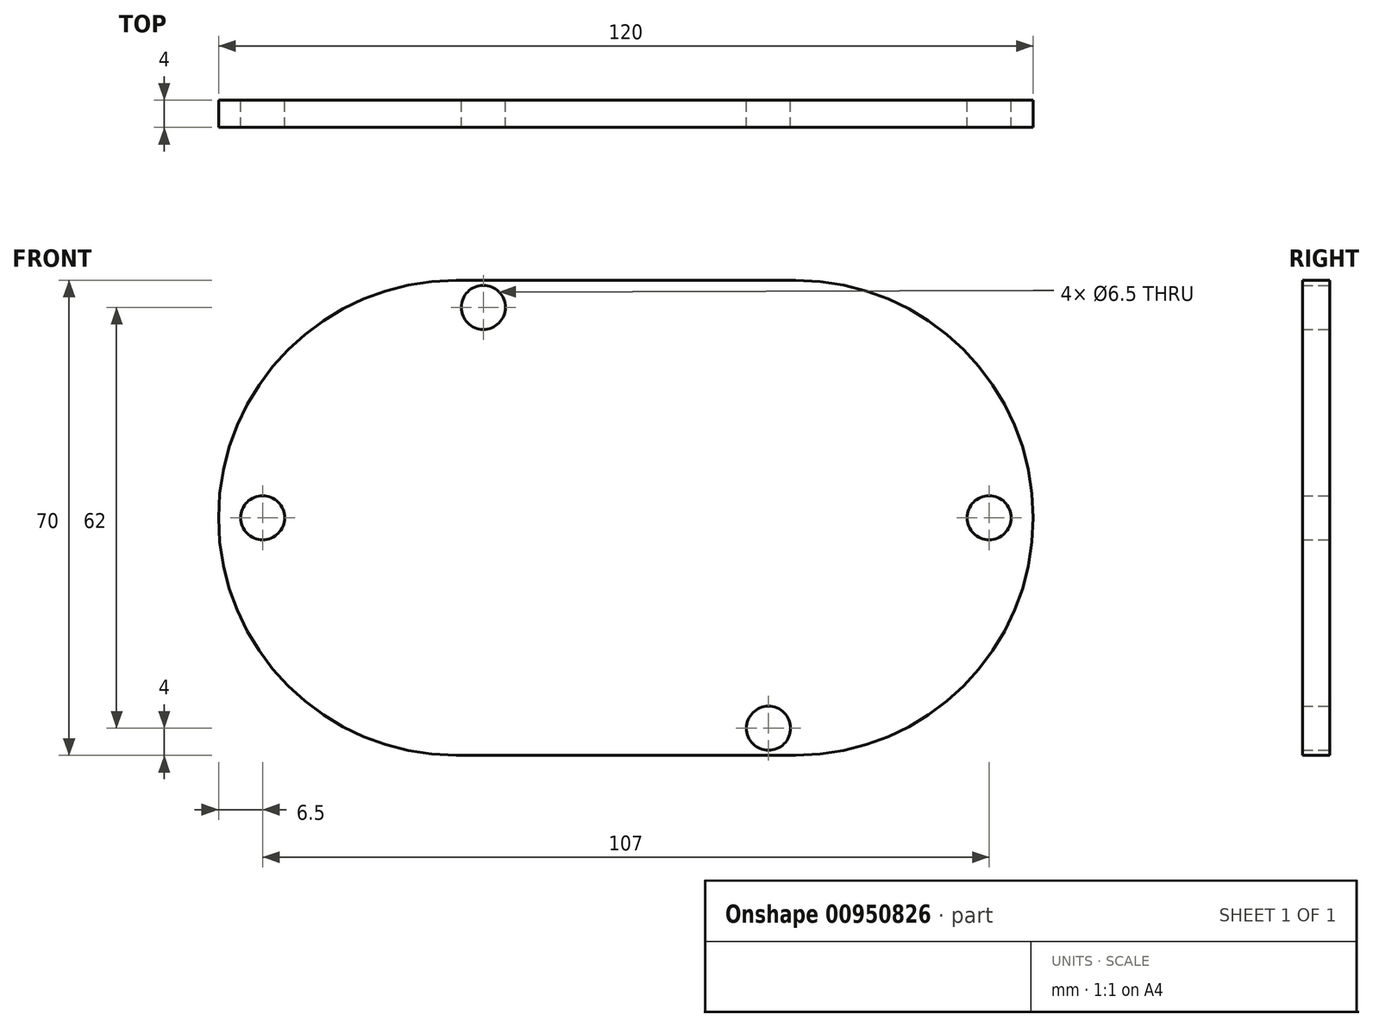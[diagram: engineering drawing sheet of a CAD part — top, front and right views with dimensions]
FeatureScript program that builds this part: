
annotation { "Feature Type Name" : "Feature", "Feature Type Description" : "" }
export const myFeature = defineFeature(function(context is Context, id is Id, definition is map)
    precondition{}
    {
        {
            var Q0;
            Q0=qCreatedBy(makeId("Front.planeOp"),FACE);
            var sketch = newSketch(context, id + "F0", { "sketchPlane" : qUnion([Q0])});
            skLineSegment(sketch, "E0", {"start": v(-25, 35) * mm, "end": v(25, 35) * mm});
            skLineSegment(sketch, "E1", {"start": v(-25, -35) * mm, "end": v(25, -35) * mm});
            skArc(sketch, "E2", {"start": v(25, -35) * mm, "mid": v(60, 0) * mm, "end": v(25, 35) * mm});
            skArc(sketch, "E3", {"start": v(-25, 35) * mm, "mid": v(-60, 0) * mm, "end": v(-25, -35) * mm});
            skSolve(sketch);
        }
        {
            var Q0;
            Q0=qSketchRegion(id+"F0",true);
            extrude(context, id + "F1", {"entities" : qUnion([Q0]), "depth" : 4 * mm, "offsetDistance" : 25 * mm});
        }
        {
            var Q0;
            Q0=qCreatedBy(makeId("Front.planeOp"),FACE);
            var sketch = newSketch(context, id + "F2", { "sketchPlane" : qUnion([Q0])});
            skCircle(sketch, "E4", {"center": v(-21, 31) * mm, "radius": 3.25 * mm});
            skCircle(sketch, "E5", {"center": v(21, -31) * mm, "radius": 3.25 * mm});
            skCircle(sketch, "E6", {"center": v(53.5, 0) * mm, "radius": 3.25 * mm});
            skCircle(sketch, "E7", {"center": v(-53.5, 0) * mm, "radius": 3.25 * mm});
            skSolve(sketch);
        }
        {
            var Q0;
            Q0=qSketchRegion(id+"F2",true);
            extrude(context, id + "F3", {"entities" : qUnion([Q0]), "operationType" : NewBodyOperationType.REMOVE, "endBound" : BoundingType.THROUGH_ALL, "depth" : 25 * mm, "offsetDistance" : 25 * mm});
        }
    });
